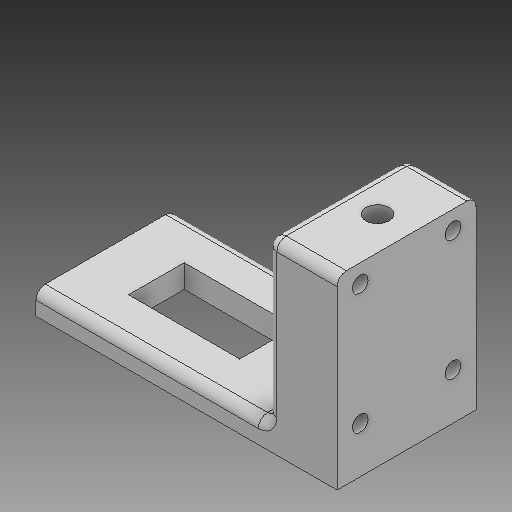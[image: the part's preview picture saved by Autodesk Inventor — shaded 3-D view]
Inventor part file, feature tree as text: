
AUTODESK INVENTOR PART (.ipt)
format: ipt  version: 2018 (Build 220112000, 112)  size: 143,360 bytes
history: native  units: mm
features: sketch x5, other x3
ambient origin geometry x8: Origin, YZ Plane, XZ Plane, XY Plane, X Axis, Y Axis, Z Axis, Center Point
bodies: Volumenkörper1 (feature_tree)
feature tree (8):
  other  "L-Halterung Servo.ipt"
  other  "Volumenkörper1::L-Halterung Servo.ipt"
  other  "Bezeichnung1"
  sketch  "Skizze1"  dims[d0=10.0mm]
  sketch  "Skizze2"
  sketch  "Skizze3"
  sketch  "Skizze4"
  sketch  "Skizze5"
